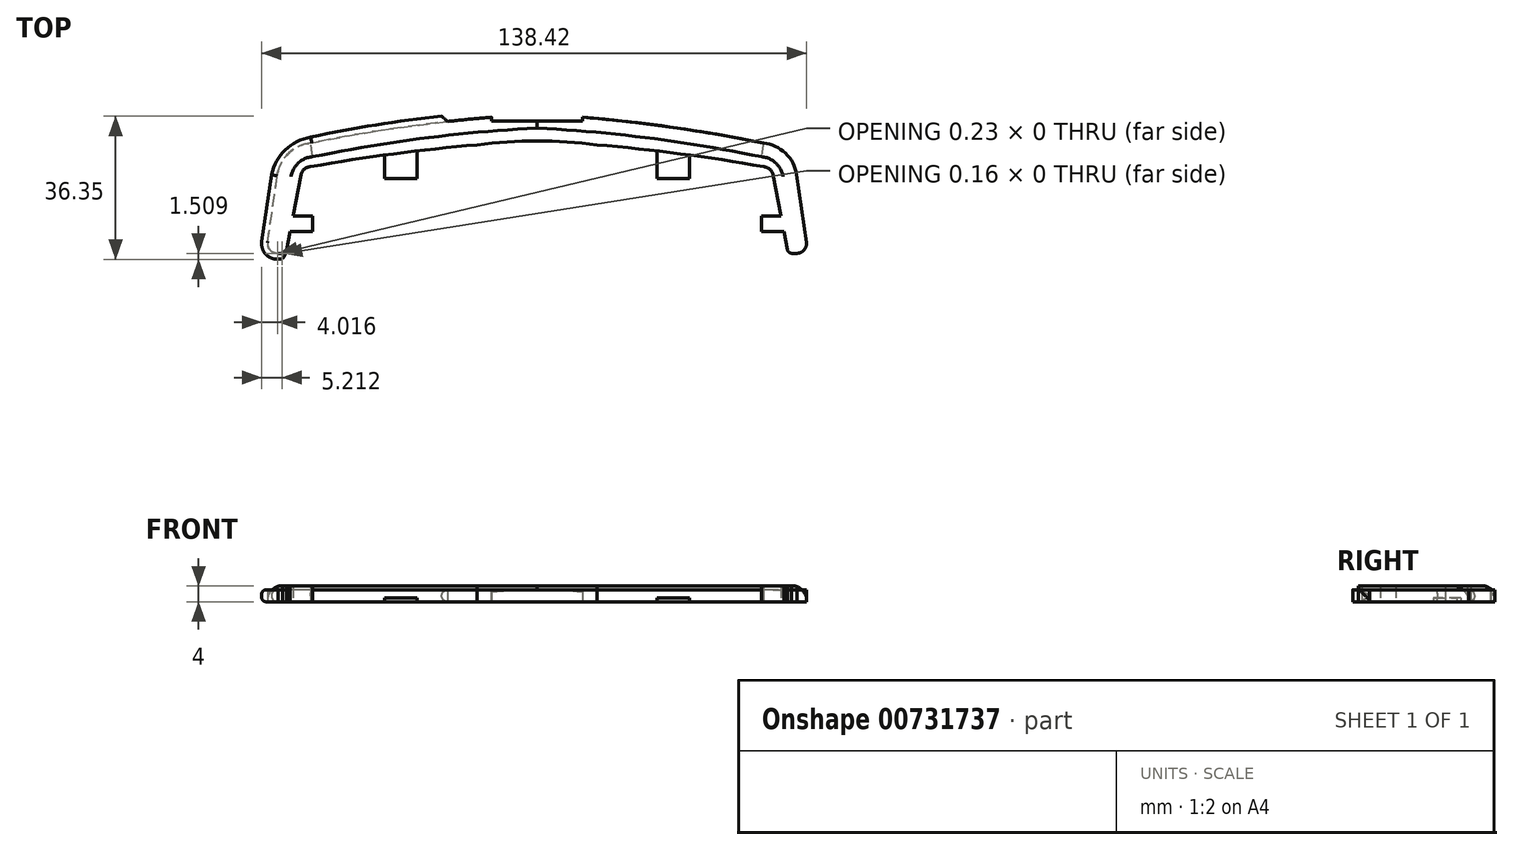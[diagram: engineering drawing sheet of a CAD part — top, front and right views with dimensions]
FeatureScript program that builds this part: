
annotation { "Feature Type Name" : "Feature", "Feature Type Description" : "" }
export const myFeature = defineFeature(function(context is Context, id is Id, definition is map)
    precondition{}
    {
        {
            var Q0;
            Q0=qCreatedBy(makeId("Top.planeOp"),FACE);
            var sketch = newSketch(context, id + "F0", { "sketchPlane" : qUnion([Q0])});
            skLineSegment(sketch, "E0", {"start": v(-57.5, -40) * mm, "end": v(0, -32.43) * mm, "construction": true});
            skLineSegment(sketch, "E1", {"start": v(0, -32.43) * mm, "end": v(57.5, -40) * mm, "construction": true});
            skLineSegment(sketch, "E2", {"start": v(-57.5, -40) * mm, "end": v(57.5, -40) * mm, "construction": true});
            skPoint(sketch, "E3", {"position": v(0, -40) * mm});
            skPoint(sketch, "E4", {"position": v(0, -33.43) * mm});
            skPoint(sketch, "E5", {"position": v(0, -28.43) * mm});
            skLineSegment(sketch, "E6", {"start": v(0, -28.43) * mm, "end": v(-11.5, -28.43) * mm});
            skLineSegment(sketch, "E7", {"start": v(-11.5, -28.43) * mm, "end": v(-11.5, -27.43) * mm});
            skLineSegment(sketch, "E8", {"start": v(-30.5, -35.99) * mm, "end": v(-30.5, -43.03) * mm});
            skLineSegment(sketch, "E9", {"start": v(-30.5, -43.03) * mm, "end": v(-38.7, -43.03) * mm});
            skLineSegment(sketch, "E10", {"start": v(-38.7, -43.03) * mm, "end": v(-38.7, -37.03) * mm});
            skPoint(sketch, "E11", {"position": v(-59.56, -40) * mm});
            skLineSegment(sketch, "E12", {"start": v(-59.95, -42.02) * mm, "end": v(-63.68, -61.17) * mm});
            skPoint(sketch, "E13", {"position": v(-62, -52.5) * mm});
            skLineSegment(sketch, "E14", {"start": v(-62, -52.5) * mm, "end": v(-57, -52.5) * mm});
            skLineSegment(sketch, "E15", {"start": v(-57, -52.5) * mm, "end": v(-57, -56.5) * mm});
            skLineSegment(sketch, "E16", {"start": v(-57, -56.5) * mm, "end": v(-62.77, -56.5) * mm});
            skLineSegment(sketch, "E17", {"start": v(-64.68, -62) * mm, "end": v(-66.07, -62) * mm});
            skPoint(sketch, "E18", {"position": v(-57.5, -42.5) * mm});
            skArc(sketch, "E19", {"start": v(-57.5, -40) * mm, "mid": v(-59.1, -40.57) * mm, "end": v(-59.95, -42.02) * mm});
            skPoint(sketch, "E20", {"position": v(-57.5, -34) * mm});
            skArc(sketch, "E21", {"start": v(-11.5, -27.43) * mm, "mid": v(-34.6, -30) * mm, "end": v(-57.5, -34) * mm});
            skLineSegment(sketch, "E22", {"start": v(-68.44, -59.26) * mm, "end": v(-65.95, -42.02) * mm});
            skArc(sketch, "E23", {"start": v(-57.5, -34) * mm, "mid": v(-63.12, -36.54) * mm, "end": v(-65.95, -42.02) * mm});
            skPoint(sketch, "E24", {"position": v(-68.4, -59.03) * mm});
            skPoint(sketch, "E25", {"position": v(-65.84, -62) * mm});
            skPoint(sketch, "E26", {"position": v(-64.84, -62) * mm});
            skPoint(sketch, "E27", {"position": v(-63.65, -61.02) * mm});
            skArc(sketch, "E28", {"start": v(-64.84, -62) * mm, "mid": v(-64.05, -61.75) * mm, "end": v(-63.65, -61.02) * mm});
            skArc(sketch, "E29", {"start": v(-68.4, -59.03) * mm, "mid": v(-67.84, -61.14) * mm, "end": v(-65.84, -62) * mm});
            skPoint(sketch, "E30.orphan", {"position": v(-68.84, -62) * mm});
            skPoint(sketch, "E31.orphan", {"position": v(-63.84, -62) * mm});
            skLineSegment(sketch, "E32.MirrorCS", {"start": v(0, -28.43) * mm, "end": v(11.5, -28.43) * mm});
            skLineSegment(sketch, "E33.MirrorCS", {"start": v(11.5, -28.43) * mm, "end": v(11.5, -27.43) * mm});
            skArc(sketch, "E34.MirrorCS", {"start": v(11.5, -27.43) * mm, "mid": v(34.6, -30) * mm, "end": v(57.5, -34) * mm});
            skArc(sketch, "E35.MirrorCS", {"start": v(57.5, -34) * mm, "mid": v(63.12, -36.54) * mm, "end": v(65.95, -42.02) * mm});
            skArc(sketch, "E36.MirrorCS", {"start": v(57.5, -40) * mm, "mid": v(59.1, -40.57) * mm, "end": v(59.95, -42.02) * mm});
            skLineSegment(sketch, "E37.MirrorCS", {"start": v(68.44, -59.26) * mm, "end": v(65.95, -42.02) * mm});
            skLineSegment(sketch, "E38.MirrorCS", {"start": v(59.95, -42.02) * mm, "end": v(63.68, -61.17) * mm});
            skLineSegment(sketch, "E39.MirrorCS", {"start": v(57, -56.5) * mm, "end": v(62.77, -56.5) * mm});
            skLineSegment(sketch, "E40.MirrorCS", {"start": v(57, -52.5) * mm, "end": v(57, -56.5) * mm});
            skLineSegment(sketch, "E41.MirrorCS", {"start": v(62, -52.5) * mm, "end": v(57, -52.5) * mm});
            skLineSegment(sketch, "E42.MirrorCS", {"start": v(38.7, -43.03) * mm, "end": v(38.7, -37.03) * mm});
            skLineSegment(sketch, "E43.MirrorCS", {"start": v(30.5, -43.03) * mm, "end": v(38.7, -43.03) * mm});
            skLineSegment(sketch, "E44.MirrorCS", {"start": v(30.5, -35.99) * mm, "end": v(30.5, -43.03) * mm});
            skArc(sketch, "E45.MirrorCS", {"start": v(68.4, -59.03) * mm, "mid": v(67.84, -61.14) * mm, "end": v(65.84, -62) * mm});
            skLineSegment(sketch, "E46.MirrorCS", {"start": v(64.68, -62) * mm, "end": v(66.07, -62) * mm});
            skArc(sketch, "E47.MirrorCS", {"start": v(64.84, -62) * mm, "mid": v(64.05, -61.75) * mm, "end": v(63.65, -61.02) * mm});
            skLineSegment(sketch, "E48", {"start": v(-15.2, -34.43) * mm, "end": v(15.2, -34.43) * mm, "construction": true});
            skPoint(sketch, "E49", {"position": v(-15.2, -34.43) * mm});
            skPoint(sketch, "E50", {"position": v(15.2, -34.43) * mm});
            skArc(sketch, "E51", {"start": v(15.2, -34.43) * mm, "mid": v(0, -33.43) * mm, "end": v(-15.2, -34.43) * mm});
            skArc(sketch, "E52", {"start": v(-15.2, -34.43) * mm, "mid": v(-36.41, -36.73) * mm, "end": v(-57.5, -40) * mm});
            skArc(sketch, "E53.MirrorCS", {"start": v(15.2, -34.43) * mm, "mid": v(36.41, -36.73) * mm, "end": v(57.5, -40) * mm});
            skLineSegment(sketch, "E54", {"start": v(-20.25, -26.73) * mm, "end": v(20.25, -26.73) * mm, "construction": true});
            skPoint(sketch, "E55", {"position": v(0, -26.73) * mm});
            skPoint(sketch, "E56", {"position": v(-57.5, -32.5) * mm});
            skPoint(sketch, "E57", {"position": v(-24.23, -27.16) * mm});
            skPoint(sketch, "E58", {"position": v(-67.45, -42.02) * mm});
            skPoint(sketch, "E59", {"position": v(-69.92, -59.03) * mm});
            skArc(sketch, "E60", {"start": v(-24.23, -27.16) * mm, "mid": v(-40.94, -29.37) * mm, "end": v(-57.5, -32.5) * mm});
            skArc(sketch, "E61", {"start": v(-57.5, -32.5) * mm, "mid": v(-63.96, -35.7) * mm, "end": v(-67.45, -42.02) * mm});
            skLineSegment(sketch, "E62", {"start": v(-67.45, -42.02) * mm, "end": v(-69.92, -59.03) * mm});
            skPoint(sketch, "E63", {"position": v(-65.84, -63.5) * mm});
            skPoint(sketch, "E64", {"position": v(-64.68, -63.5) * mm});
            skLineSegment(sketch, "E65", {"start": v(-64.68, -63.5) * mm, "end": v(-65.84, -63.5) * mm});
            skArc(sketch, "E66", {"start": v(-69.92, -59.03) * mm, "mid": v(-68.94, -62.23) * mm, "end": v(-65.84, -63.5) * mm});
            skArc(sketch, "E67", {"start": v(-64.68, -63.5) * mm, "mid": v(-64.05, -62.4) * mm, "end": v(-63.68, -61.17) * mm});
            skPoint(sketch, "E68", {"position": v(-22.73, -28.5) * mm});
            skArc(sketch, "E69.MirrorCS", {"start": v(24.23, -27.16) * mm, "mid": v(40.94, -29.37) * mm, "end": v(57.5, -32.5) * mm});
            skArc(sketch, "E70.MirrorCS", {"start": v(57.5, -32.5) * mm, "mid": v(63.96, -35.7) * mm, "end": v(67.45, -42.02) * mm});
            skLineSegment(sketch, "E71.MirrorCS", {"start": v(67.45, -42.02) * mm, "end": v(69.92, -59.03) * mm});
            skArc(sketch, "E72.MirrorCS", {"start": v(69.92, -59.03) * mm, "mid": v(68.94, -62.23) * mm, "end": v(65.84, -63.5) * mm});
            skLineSegment(sketch, "E73.MirrorCS", {"start": v(64.68, -63.5) * mm, "end": v(65.84, -63.5) * mm});
            skArc(sketch, "E74.MirrorCS", {"start": v(64.68, -63.5) * mm, "mid": v(64.05, -62.4) * mm, "end": v(63.68, -61.17) * mm});
            skLineSegment(sketch, "E75", {"start": v(-24.23, -27.16) * mm, "end": v(-22.73, -28.5) * mm});
            skLineSegment(sketch, "E76.MirrorCS", {"start": v(24.23, -27.16) * mm, "end": v(22.73, -28.5) * mm});
            skSolve(sketch);
        }
        {
            var Q0;
            Q0=makeQuery(id+"F0.imprint","IMPRINT",FACE,{"disambiguationData":[TD([[makeQuery(id+"F0.imprint","IMPRINT",EDGE,{"derivedFrom":sQuery(id+"F0.wireOp",EDGE,"E6")}),1.0]])]});
            var Q1;
            {var subQ0=sQuery(id+"F0.wireOp",EDGE,"E14");Q1=makeQuery(id+"F0.imprint","IMPRINT",FACE,{"disambiguationData":[TD([[makeQuery(id+"F0.imprint","IMPRINT",EDGE,{"derivedFrom":subQ0}),-1.0]])]});}
            var Q2;
            {var subQ0=sQuery(id+"F0.wireOp",EDGE,"E39.MirrorCS");Q2=makeQuery(id+"F0.imprint","IMPRINT",FACE,{"disambiguationData":[TD([[makeQuery(id+"F0.imprint","IMPRINT",EDGE,{"derivedFrom":subQ0}),1.0]])]});}
            extrude(context, id + "F1", {"entities" : qUnion([Q0, Q1, Q2]), "depth" : 4 * mm, "offsetDistance" : 25 * mm});
        }
        {
            var Q0;
            {var subQ0=sQuery(id+"F0.wireOp",EDGE,"E8");Q0=makeQuery(id+"F0.imprint","IMPRINT",FACE,{"disambiguationData":[TD([[makeQuery(id+"F0.imprint","IMPRINT",EDGE,{"derivedFrom":subQ0}),-1.0]])]});}
            var Q1;
            {var subQ0=sQuery(id+"F0.wireOp",EDGE,"E42.MirrorCS");Q1=makeQuery(id+"F0.imprint","IMPRINT",FACE,{"disambiguationData":[TD([[makeQuery(id+"F0.imprint","IMPRINT",EDGE,{"derivedFrom":subQ0}),1.0]])]});}
            extrude(context, id + "F2", {"entities" : qUnion([Q0, Q1]), "operationType" : NewBodyOperationType.ADD, "depth" : 1 * mm, "offsetDistance" : 25 * mm});
        }
        {
            var Q0;
            Q0=makeQuery(id+"F1.opExtrude","CAP_EDGE",EDGE,{"disambiguationData":[OSD([sQuery(id+"F0.wireOp",EDGE,"E34.MirrorCS")])],"isStart":false});
            var Q1;
            Q1=makeQuery(id+"F1.opExtrude","CAP_EDGE",EDGE,{"disambiguationData":[OSD([sQuery(id+"F0.wireOp",EDGE,"E35.MirrorCS")])],"isStart":false});
            var Q2;
            Q2=makeQuery(id+"F1.opExtrude","CAP_EDGE",EDGE,{"disambiguationData":[OSD([sQuery(id+"F0.wireOp",EDGE,"E21")])],"isStart":false});
            var Q3;
            Q3=makeQuery(id+"F1.opExtrude","CAP_EDGE",EDGE,{"disambiguationData":[OSD([sQuery(id+"F0.wireOp",EDGE,"E23")])],"isStart":false});
            fillet(context, id + "F3", {"entities" : qUnion([Q0, Q1, Q2, Q3]), "radius" : 3.5 * mm, "tangentPropagation" : true, "rho" : 0.3, "crossSection" : FilletCrossSection.CONIC, "allowEdgeOverflow" : false});
        }
        {
            var Q0;
            {var subQ12=sQuery(id+"F0.wireOp",EDGE,"E23");Q0=makeQuery(id+"F0.imprint","IMPRINT",FACE,{"disambiguationData":[TD([[makeQuery(id+"F0.imprint","IMPRINT",EDGE,{"derivedFrom":subQ12}),-1.0]])]});}
            var Q1;
            {var subQ12=sQuery(id+"F0.wireOp",EDGE,"E35.MirrorCS");Q1=makeQuery(id+"F0.imprint","IMPRINT",FACE,{"disambiguationData":[TD([[makeQuery(id+"F0.imprint","IMPRINT",EDGE,{"derivedFrom":subQ12}),1.0]])]});}
            var Q2;
            Q2=makeQuery(id+"F0.imprint","IMPRINT",FACE,{"disambiguationData":[TD([[makeQuery(id+"F0.imprint","IMPRINT",EDGE,{"derivedFrom":sQuery(id+"F0.wireOp",EDGE,"E6")}),1.0]])]});
            extrude(context, id + "F4", {"entities" : qUnion([Q0, Q1, Q2]), "depth" : 3 * mm, "offsetDistance" : 25 * mm});
        }
        {
            var Q0;
            Q0=makeQuery(id+"F4.opExtrude","CAP_EDGE",EDGE,{"disambiguationData":[OSD([sQuery(id+"F0.wireOp",EDGE,"E60")])],"isStart":true});
            var Q1;
            Q1=makeQuery(id+"F4.opExtrude","CAP_EDGE",EDGE,{"disambiguationData":[OSD([sQuery(id+"F0.wireOp",EDGE,"E61")])],"isStart":true});
            var Q2;
            Q2=makeQuery(id+"F4.opExtrude","CAP_EDGE",EDGE,{"disambiguationData":[OSD([sQuery(id+"F0.wireOp",EDGE,"E69.MirrorCS")])],"isStart":true});
            var Q3;
            Q3=makeQuery(id+"F4.opExtrude","CAP_EDGE",EDGE,{"disambiguationData":[OSD([sQuery(id+"F0.wireOp",EDGE,"E70.MirrorCS")])],"isStart":true});
            fillet(context, id + "F5", {"entities" : qUnion([Q0, Q1, Q2, Q3]), "radius" : 1.5 * mm, "tangentPropagation" : true, "allowEdgeOverflow" : false});
        }
        {
            var Q0;
            Q0=makeQuery(id+"F4.opExtrude","CAP_EDGE",EDGE,{"disambiguationData":[OSD([sQuery(id+"F0.wireOp",EDGE,"E60")])],"isStart":false});
            var Q1;
            Q1=makeQuery(id+"F4.opExtrude","CAP_EDGE",EDGE,{"disambiguationData":[OSD([sQuery(id+"F0.wireOp",EDGE,"E61")])],"isStart":false});
            var Q2;
            Q2=makeQuery(id+"F4.opExtrude","CAP_EDGE",EDGE,{"disambiguationData":[OSD([sQuery(id+"F0.wireOp",EDGE,"E69.MirrorCS")])],"isStart":false});
            var Q3;
            Q3=makeQuery(id+"F4.opExtrude","CAP_EDGE",EDGE,{"disambiguationData":[OSD([sQuery(id+"F0.wireOp",EDGE,"E70.MirrorCS")])],"isStart":false});
            fillet(context, id + "F6", {"entities" : qUnion([Q0, Q1, Q2, Q3]), "radius" : 1.5 * mm, "tangentPropagation" : true, "allowEdgeOverflow" : false});
        }
    });
